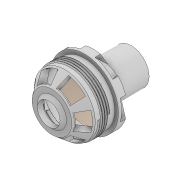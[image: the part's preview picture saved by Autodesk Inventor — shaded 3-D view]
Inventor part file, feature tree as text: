
AUTODESK INVENTOR PART (.ipt)
format: ipt  version: 2020 (Build 240168000, 168)  size: 610,304 bytes
history: native  units: mm
features: sketch x18, extrude x11, chamfer x7, revolve x5, projected_geometry x5, plane x4, helix x2, pattern_circular x2, split x1
ambient origin geometry x8: Origin, YZ Plane, XZ Plane, XY Plane, X Axis, Y Axis, Z Axis, Center Point
bodies: Solid1 (feature_tree)
feature tree (55):
  extrude  "Extrusion1"  Depth=2.0mm
  chamfer  "Chamfer1"  Distance=2.0mm
  revolve  "Revolution1"  [1 undecoded]
  extrude  "Extrusion2"  Depth=18.75mm
  sketch  "Sketch6"  dims[d17=1.6mm]
  helix  "Coil2"  [1 undecoded]
  chamfer  "Chamfer4"  Distance=10.0mm
  chamfer  "Chamfer5"  Distance=0.65mm Angle=45.0deg
  extrude  "Extrusion4"  Depth=42.0mm
  extrude  "Extrusion6"  Depth=3.3mm
  extrude  "Extrusion7"  Depth=1.2mm
  helix  "Coil3"  [1 undecoded]
  extrude  "Extrusion8"  Depth=3.0mm TaperAngle=0.0deg
  revolve  "Revolution2"  [1 undecoded]
  plane  "Work Plane2"
  split  "Split1"
  revolve  "Revolution3"  [1 undecoded]
  plane  "Work Plane3"
  plane  "Work Plane4"
  extrude  "Extrusion10"  Depth=10.0mm
  extrude  "Extrusion11"  Depth=10.0mm TaperAngle=0.0deg
  revolve  "Revolution4"  Angle=135.0deg
  extrude  "Extrusion12"  TaperAngle=90.0deg  [1 undecoded]
  revolve  "Revolution5"  [1 undecoded]
  plane  "Work Plane5"
  extrude  "Extrusion13"  Depth=10.0mm
  chamfer  "Chamfer7"  Distance=20.0mm
  pattern_circular  "Circular Pattern2"  [2 undecoded]
  extrude  "Extrusion15"  Depth=10.0mm
  pattern_circular  "Circular Pattern4"  Angle=90.0deg  [1 undecoded]
  chamfer  "Chamfer8"  [1 undecoded]
  chamfer  "Chamfer9"  [1 undecoded]
  chamfer  "Chamfer10"  Distance=42.0mm
  sketch  "Sketch1"  dims[d0=18.0mm d1=2.0mm d2=2.0mm d3=0.0mm]
  sketch  "Sketch4"  dims[d4=2.0mm d5=2.0mm d6=45.0deg d10=12.25mm]
  sketch  "Sketch5"  dims[d11=8.0mm d12=18.75mm d14=1.5mm]
  projected_geometry  "Projected Loop1"
  sketch  "Sketch8"  dims[d18=90.0deg d19=10.0mm d20=0.0mm]
  sketch  "Sketch9"  dims[d21=1.0mm]
  sketch  "Sketch10"  dims[d22=1.0mm]
  sketch  "Sketch11"  dims[d23=1.5mm]
  sketch  "Sketch12"  dims[d24=0.8mm]
  sketch  "Sketch13"  dims[d42=0.1mm]
  sketch  "Sketch14"  dims[d43=1.5mm]
  sketch  "Sketch16"  dims[d44=6.0mm d45=10.0mm d46=0.0mm d47=90.0deg d48=90.0deg d49=0.0mm d50=0.0mm d51=0.65mm d52=4.0mm d53=45.0deg]
  sketch  "Sketch17"  dims[d54=0.65mm d55=4.0mm d56=45.0deg d57=42.0mm]
  projected_geometry  "Projected Loop3"
  sketch  "Sketch18"  dims[d58=28.0mm d59=0.0mm d60=3.3mm]
  sketch  "Sketch19"  dims[d61=1.2mm d62=1.2mm d65=12.0mm d66=0.0mm]
  sketch  "Sketch20"  dims[d67=25.0mm d68=3.0mm d69=0.0mm]
  projected_geometry  "Projected Loop4"
  projected_geometry  "Projected Loop5"
  sketch  "Sketch21"  dims[d73=1.5mm d74=1.0mm]
  projected_geometry  "Projected Loop6"
  sketch  "Sketch23"  dims[d75=0.8mm d76=1.5mm d77=28.0mm d78=10.0mm d79=0.0mm d80=90.0deg d81=90.0deg d82=0.0mm d83=0.0mm d84=45.0mm d85=20.0mm d86=0.0mm d87=135.0deg d88=90.0deg d89=0.0mm d91=11.25mm d92=20.0mm d93=11.0mm d94=1.6mm d95=90.0deg d96=-20.0mm d108=-17.3mm d109=42.0mm d110=4.8mm d111=0.0mm d112=31.068147mm d113=21.0mm d115=2.8mm d116=0.0mm d117=0.473mm d118=90.0deg d119=2.8mm d120=0.0mm d121=135.0deg d122=90.0deg d123=-32.0mm d124=4.363323mm d125=10.0mm d126=0.0mm d127=6.5mm d128=9.75mm d129=45.0deg d130=60.0mm d131=360.0deg d136=37.5mm d137=24.5mm d138=31.0mm d139=5.0mm d140=10.0mm d141=0.0mm d145=5.0mm d146=6.0mm d147=5.0mm d148=6.0mm d149=60.0mm d150=360.0deg d152=6.0mm d153=2.0mm d154=45.0deg d155=6.0mm d156=2.0mm d157=45.0deg d158=2.0mm d159=2.0mm d160=45.0deg d70=0.5mm d71=0.872665mm d72=0.5mm d90=0.872665mm]
note: 12 required parameter values undecoded (feature->parameter linkage not recoverable at this tier; creation-order binding heuristic only, values carry confidence <= 0.55)